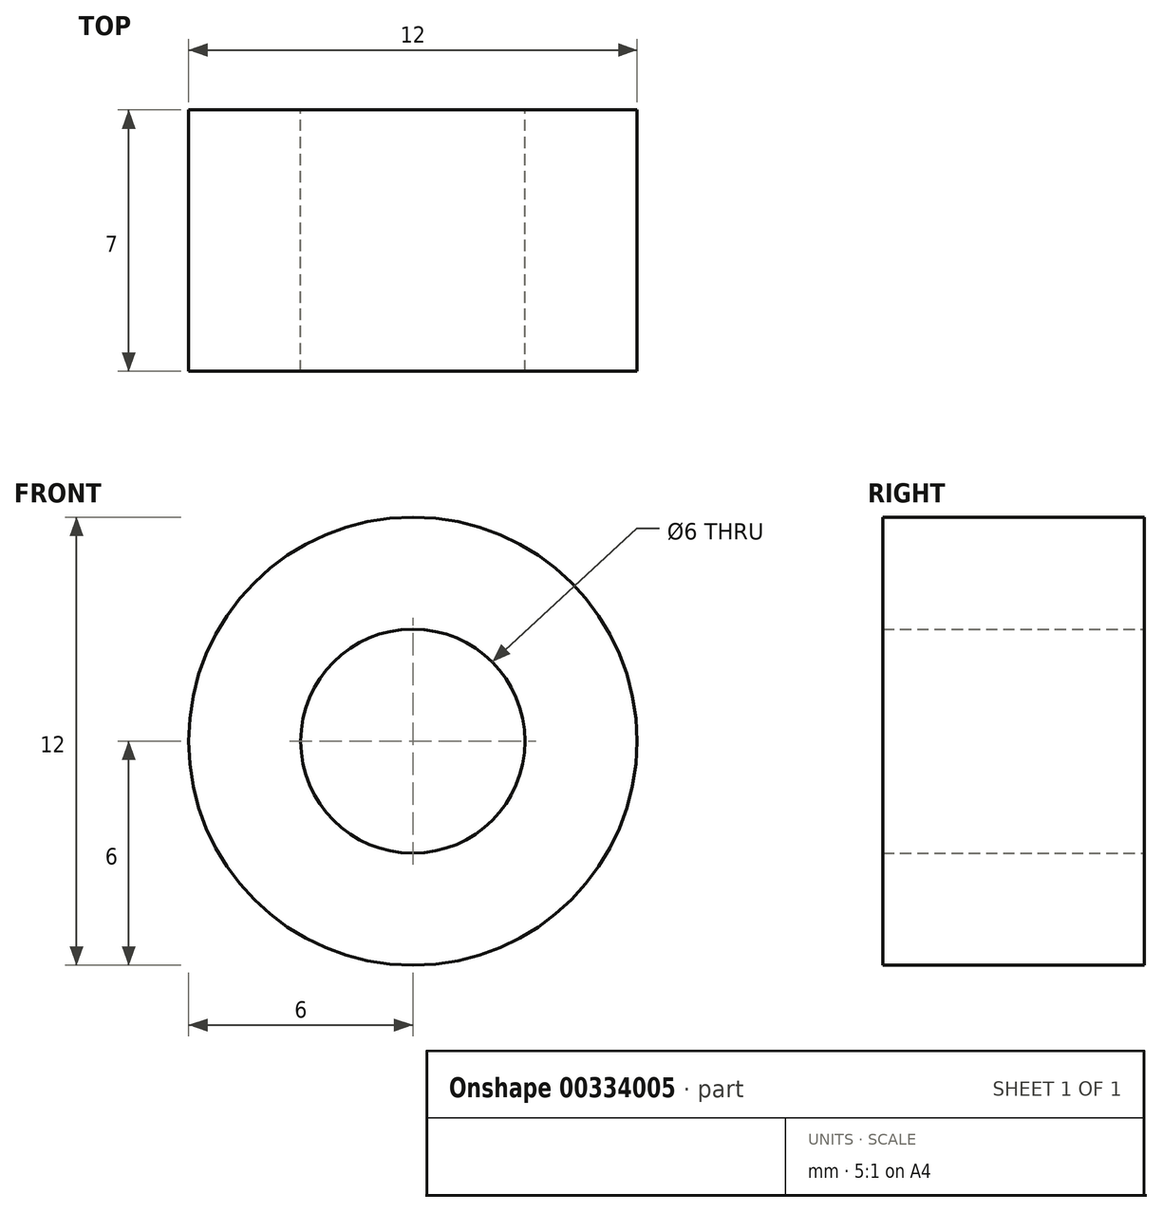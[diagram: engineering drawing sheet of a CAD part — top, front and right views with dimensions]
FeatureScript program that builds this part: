
annotation { "Feature Type Name" : "Feature", "Feature Type Description" : "" }
export const myFeature = defineFeature(function(context is Context, id is Id, definition is map)
    precondition{}
    {
        {
            var Q0;
            Q0=qCreatedBy(makeId("Front.planeOp"),FACE);
            var sketch = newSketch(context, id + "F0", { "sketchPlane" : qUnion([Q0])});
            skCircle(sketch, "E0", {"center": v(0, 0) * mm, "radius": 6 * mm});
            skCircle(sketch, "E1", {"center": v(0, 0) * mm, "radius": 3 * mm});
            skSolve(sketch);
        }
        {
            var Q0;
            Q0=makeQuery(id+"F0.imprint","IMPRINT",FACE,{"disambiguationData":[TD([[makeQuery(id+"F0.imprint","IMPRINT",EDGE,{"derivedFrom":sQuery(id+"F0.wireOp",EDGE,"E0")}),1.0]])]});
            extrude(context, id + "F1", {"entities" : qUnion([Q0]), "depth" : 7 * mm});
        }
    });
